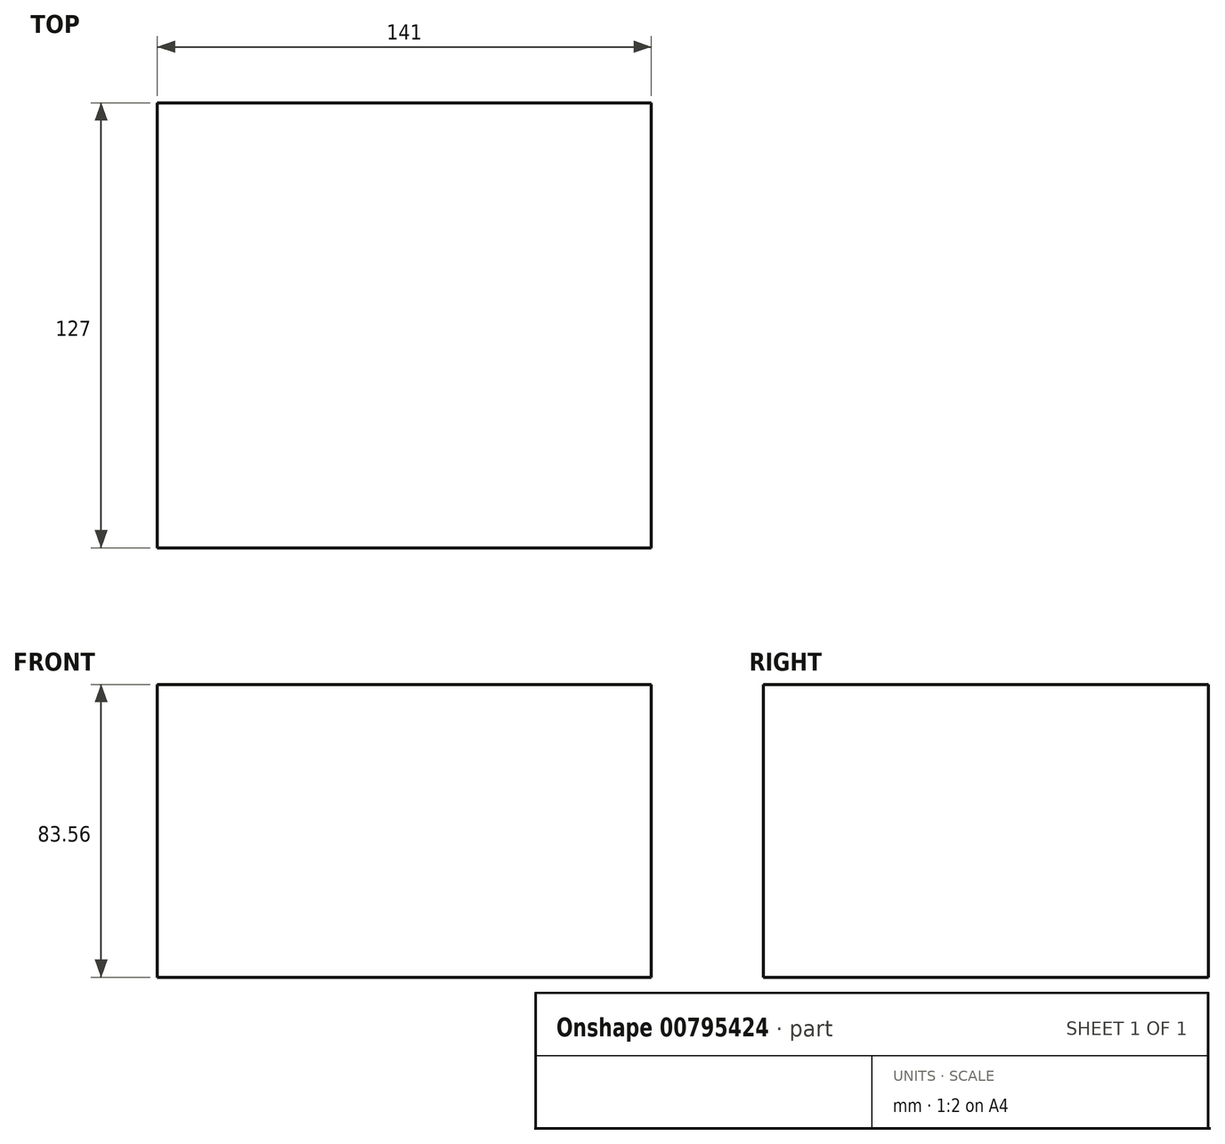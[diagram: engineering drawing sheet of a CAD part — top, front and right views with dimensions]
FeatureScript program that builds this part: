
annotation { "Feature Type Name" : "Feature", "Feature Type Description" : "" }
export const myFeature = defineFeature(function(context is Context, id is Id, definition is map)
    precondition{}
    {
        {
            var Q0;
            Q0=qCreatedBy(makeId("Front.planeOp"),FACE);
            var sketch = newSketch(context, id + "F0", { "sketchPlane" : qUnion([Q0])});
            skLineSegment(sketch, "E0.bottom", {"start": v(70.5, 41.78) * mm, "end": v(-70.5, 41.78) * mm});
            skLineSegment(sketch, "E0.top", {"start": v(70.5, -41.78) * mm, "end": v(-70.5, -41.78) * mm});
            skLineSegment(sketch, "E0.left", {"start": v(70.5, 41.78) * mm, "end": v(70.5, -41.78) * mm});
            skLineSegment(sketch, "E0.right", {"start": v(-70.5, 41.78) * mm, "end": v(-70.5, -41.78) * mm});
            skPoint(sketch, "E0.middle", {"position": v(0, 0) * mm});
            skSolve(sketch);
        }
        {
            var Q0;
            Q0=makeQuery(id+"F0.imprint","IMPRINT",FACE,{"disambiguationData":[TD([[makeQuery(id+"F0.imprint","IMPRINT",EDGE,{"derivedFrom":sQuery(id+"F0.wireOp",EDGE,"E0.bottom")}),1.0]])]});
            extrude(context, id + "F1", {"entities" : qUnion([Q0]), "depth" : 127 * mm, "offsetDistance" : 25.4 * mm});
        }
    });
